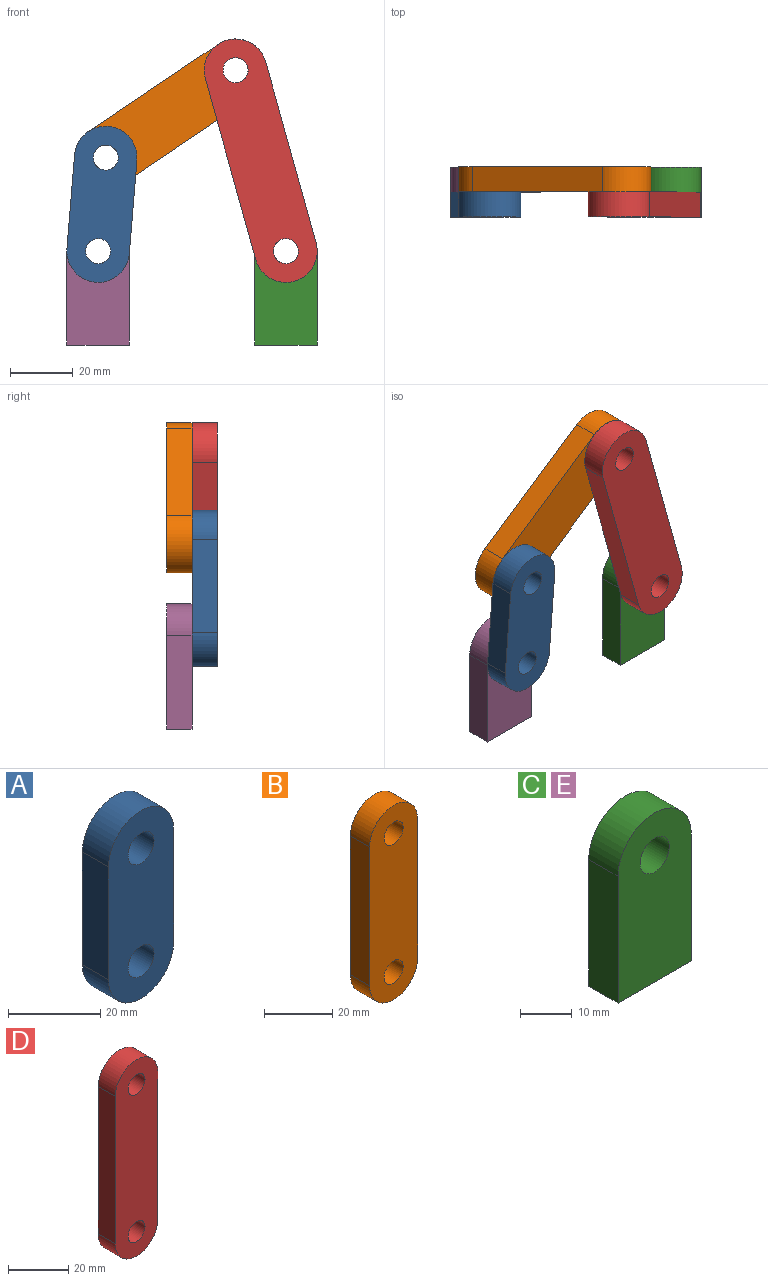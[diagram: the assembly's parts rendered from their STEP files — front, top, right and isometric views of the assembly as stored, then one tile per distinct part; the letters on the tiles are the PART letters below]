
ASSEMBLY  parts=5 mates=5
PART A: 8 faces, bbox 20x8x50 mm
  f0: cylinder r=10mm len=20mm, axis (0,1,0), area 251.3mm2, adj f1,f3,f6,f7
  f1: plane 30x8mm, normal (-1,0,0), area 240mm2, adj f0,f2,f6,f7
  f2: cylinder r=10mm len=20mm, axis (0,1,0), area 251.3mm2, adj f1,f3,f6,f7
  f3: plane 30x8mm, normal (1,0,0), area 240mm2, adj f0,f2,f6,f7
  f4: cylinder r=4mm len=8mm, axis (0,1,0), area 201.1mm2, adj f6,f7
  f5: cylinder r=4mm len=8mm, axis (0,1,0), area 201.1mm2, adj f6,f7
  f6: plane 50x20mm, normal (0,-1,0), area 813.6mm2, adj f0,f1,f2,f3,f4,f5
  f7: plane 50x20mm, normal (0,1,0), area 813.6mm2, adj f0,f1,f2,f3,f4,f5
PART B: 8 faces, bbox 20x8x70 mm
  f0: cylinder r=10mm len=20mm, axis (0,1,0), area 251.3mm2, adj f1,f3,f6,f7
  f1: plane 50x8mm, normal (-1,0,0), area 400mm2, adj f0,f2,f6,f7
  f2: cylinder r=10mm len=20mm, axis (0,1,0), area 251.3mm2, adj f1,f3,f6,f7
  f3: plane 50x8mm, normal (1,0,0), area 400mm2, adj f0,f2,f6,f7
  f4: cylinder r=4mm len=8mm, axis (0,1,0), area 201.1mm2, adj f6,f7
  f5: cylinder r=4mm len=8mm, axis (0,1,0), area 201.1mm2, adj f6,f7
  f6: plane 70x20mm, normal (0,-1,0), area 1213.6mm2, adj f0,f1,f2,f3,f4,f5
  f7: plane 70x20mm, normal (0,1,0), area 1213.6mm2, adj f0,f1,f2,f3,f4,f5
PART C: 7 faces, bbox 20x8x40 mm
  f0: cylinder r=10mm len=20mm, axis (0,1,0), area 251.3mm2, adj f1,f4,f5,f6
  f1: plane 30x8mm, normal (-1,0,0), area 240mm2, adj f0,f2,f5,f6
  f2: plane 20x8mm, normal (0,0,-1), area 160mm2, adj f1,f4,f5,f6
  f3: cylinder r=4mm len=8mm, axis (0,1,0), area 201.1mm2, adj f5,f6
  f4: plane 30x8mm, normal (1,0,0), area 240mm2, adj f0,f2,f5,f6
  f5: plane 40x20mm, normal (0,-1,0), area 706.8mm2, adj f0,f1,f2,f3,f4
  f6: plane 40x20mm, normal (0,1,0), area 706.8mm2, adj f0,f1,f2,f3,f4
PART D: 8 faces, bbox 20x8x80 mm
  f0: cylinder r=10mm len=20mm, axis (0,1,0), area 251.3mm2, adj f1,f3,f6,f7
  f1: plane 60x8mm, normal (-1,0,0), area 480mm2, adj f0,f2,f6,f7
  f2: cylinder r=10mm len=20mm, axis (0,1,0), area 251.3mm2, adj f1,f3,f6,f7
  f3: plane 60x8mm, normal (1,0,0), area 480mm2, adj f0,f2,f6,f7
  f4: cylinder r=4mm len=8mm, axis (0,1,0), area 201.1mm2, adj f6,f7
  f5: cylinder r=4mm len=8mm, axis (0,1,0), area 201.1mm2, adj f6,f7
  f6: plane 80x20mm, normal (0,-1,0), area 1413.6mm2, adj f0,f1,f2,f3,f4,f5
  f7: plane 80x20mm, normal (0,1,0), area 1413.6mm2, adj f0,f1,f2,f3,f4,f5
PART E: same geometry as C
PLACE A rot(axis=(-0.04,0,-1),180deg) t=(1.21,-8,44.95)mm
PLACE B rot(axis=(0,1,0),56.1deg) t=(23.17,8,73.85)mm
PLACE C t=(60,8,0)mm
PLACE D rot(axis=(0,-1,0),15.5deg) t=(51.96,0,58.9)mm
PLACE E t=(0,8,0)mm
MATE revolute D.f2 <-> C.f0  axis (0,1,0) through (60,0,30)mm
MATE revolute A.f2 <-> E.f0  axis (0,1,0) through (0,0,30)mm
MATE revolute D.f0 <-> B.f0  axis (0,1,0) through (43.92,0,87.8)mm
MATE revolute B.f2 <-> A.f0  axis (0,-1,0) through (2.43,0,59.9)mm
MATE fastened C.f5 <-> E.f5  axis (0,-1,0) through (60,0,0)mm
